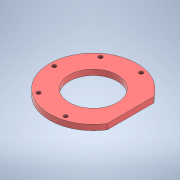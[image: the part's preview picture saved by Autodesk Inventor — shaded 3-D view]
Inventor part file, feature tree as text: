
AUTODESK INVENTOR PART (.ipt)
format: ipt  version: 2022 (Build 260153000, 153)  size: 129,024 bytes
history: native  units: mm
features: extrude x1, sketch x1
ambient origin geometry x8: Origin, YZ Plane, XZ Plane, XY Plane, X Axis, Y Axis, Z Axis, Center Point
bodies: Body1 (feature_tree)
feature tree (2):
  extrude  "Выдавливание3"  Depth=26.0mm
  sketch  "Эскиз1"
